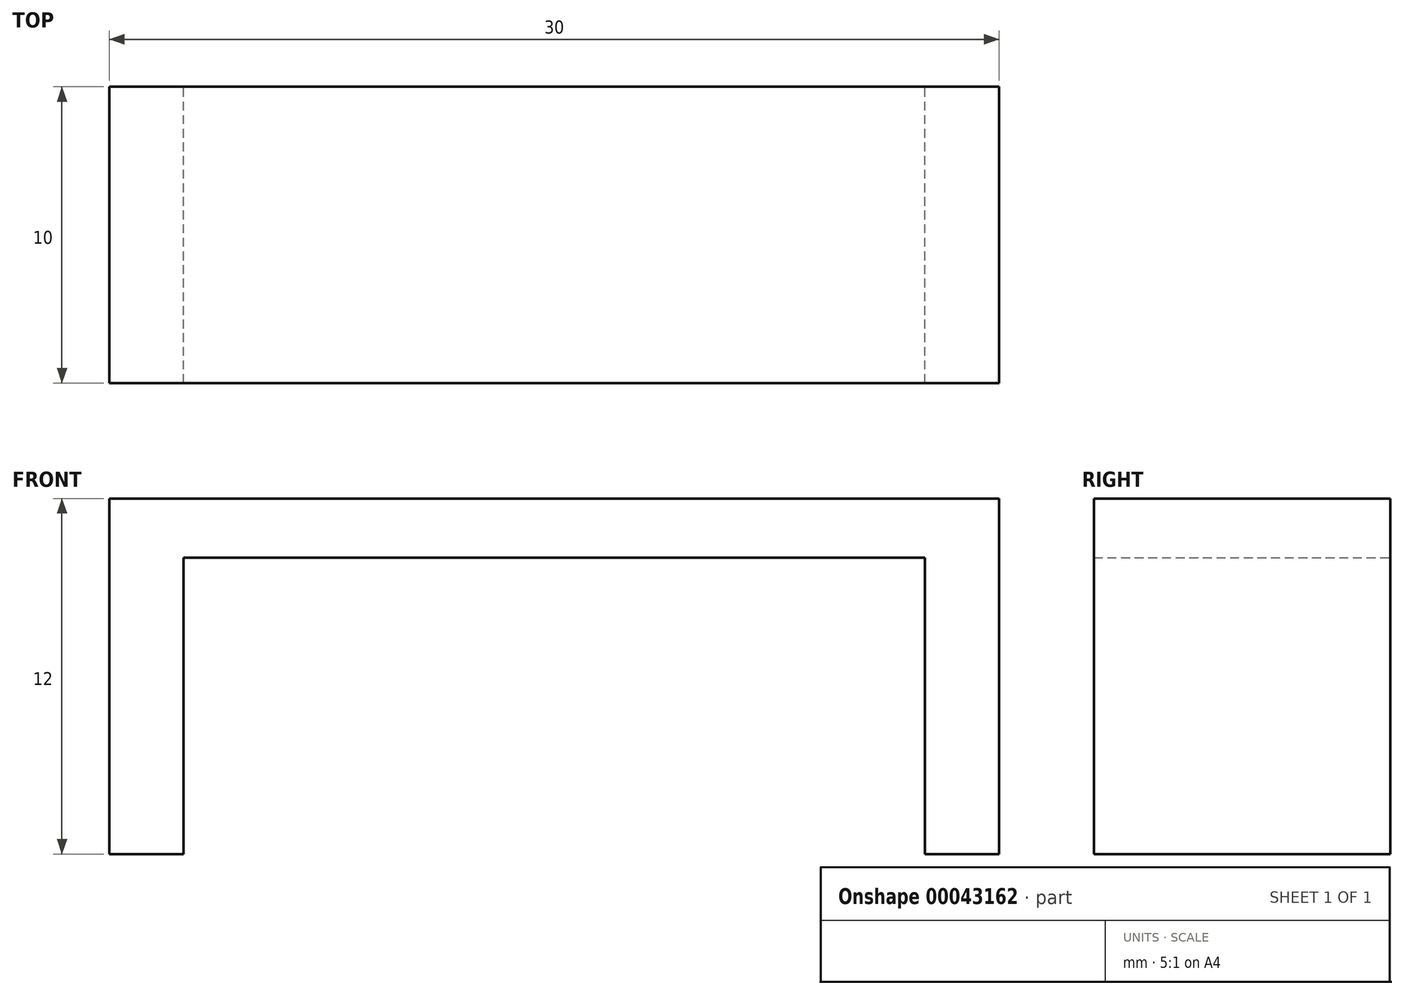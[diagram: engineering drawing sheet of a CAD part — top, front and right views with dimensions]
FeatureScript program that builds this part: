
annotation { "Feature Type Name" : "Feature", "Feature Type Description" : "" }
export const myFeature = defineFeature(function(context is Context, id is Id, definition is map)
    precondition{}
    {
        {
            var Q0;
            Q0=qCreatedBy(makeId("Front.planeOp"),FACE);
            var sketch = newSketch(context, id + "F0", { "sketchPlane" : qUnion([Q0])});
            skLineSegment(sketch, "E0", {"start": v(0, 0) * mm, "end": v(0, 12) * mm});
            skLineSegment(sketch, "E1", {"start": v(0, 12) * mm, "end": v(30, 12) * mm});
            skLineSegment(sketch, "E2", {"start": v(30, 12) * mm, "end": v(30, 0) * mm});
            skLineSegment(sketch, "E3", {"start": v(30, 0) * mm, "end": v(27.5, 0) * mm});
            skLineSegment(sketch, "E4", {"start": v(27.5, 0) * mm, "end": v(27.5, 10) * mm});
            skLineSegment(sketch, "E5", {"start": v(27.5, 10) * mm, "end": v(2.5, 10) * mm});
            skLineSegment(sketch, "E6", {"start": v(2.5, 10) * mm, "end": v(2.5, 0) * mm});
            skLineSegment(sketch, "E7", {"start": v(2.5, 0) * mm, "end": v(0, 0) * mm});
            skSolve(sketch);
        }
        {
            var Q0;
            Q0=makeQuery(id+"F0.imprint","IMPRINT",FACE,{"disambiguationData":[TD([[makeQuery(id+"F0.imprint","IMPRINT",EDGE,{"derivedFrom":sQuery(id+"F0.wireOp",EDGE,"E0")}),-1.0]])]});
            extrude(context, id + "F1", {"entities" : qUnion([Q0]), "depth" : 10 * mm});
        }
    });
